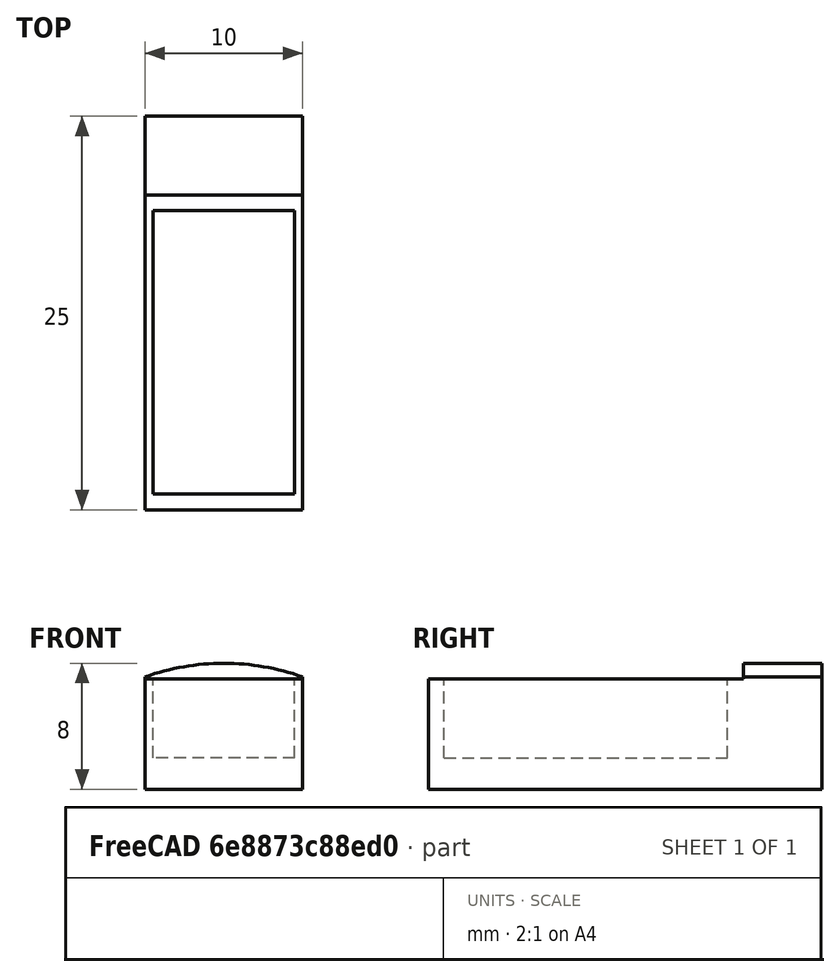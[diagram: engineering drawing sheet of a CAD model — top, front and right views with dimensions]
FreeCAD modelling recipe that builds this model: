
FCSTD DOCUMENT  (FreeCAD 0.16R4924 (Git))
Label: pin_v3
License: All rights reserved
LicenseURL: http://en.wikipedia.org/wiki/All_rights_reserved
objects: Part::Feature×9, Part::Box×3, Part::Cylinder×1, Part::MultiCommon×1, Part::MultiFuse×1, Part::Fuse×1, Part::Cut×1
note: 17 computed .brp shape members not serialized (recipe doc carries the construction recipe); baked Part::Feature solids carry a one-line shape summary decoded from their .brp

FEATURE [Part::Cylinder] Cylinder  label="rounded_top"
  Angle = 360
  Height = 30
  Placement = pos=(5,25,-7) rot=(1,0,0;1.5708rad)
  Radius = 15
FEATURE [Part::Box] Box  label="pin"
  Height = 8
  Length = 10
  Width = 30
FEATURE [Part::MultiCommon] Common  label="rounded pin"
  Shapes = -> [Cylinder,Box]
FEATURE [Part::Box] cube
  Height = 5
  Length = 18
  Placement = pos=(-9,-4.5,-2.5) rot=(0,0,1;0rad)
  Width = 9
FEATURE [Part::Feature] polyhedron
  Placement = pos=(-8.24512,0,2.5) rot=(0,0,1;0rad)
  shape: bbox 1.51 x 9 x 1.337 mm, 6 faces (baked)
FEATURE [Part::Feature] polyhedron001
  Placement = pos=(-6.24512,0,2.5) rot=(0,0,1;0rad)
  shape: bbox 1.51 x 9 x 1.337 mm, 6 faces (baked)
FEATURE [Part::Feature] polyhedron002
  Placement = pos=(-4.24512,0,2.5) rot=(0,0,1;0rad)
  shape: bbox 1.51 x 9 x 1.337 mm, 6 faces (baked)
FEATURE [Part::Feature] polyhedron003
  Placement = pos=(-2.24512,0,2.5) rot=(0,0,1;0rad)
  shape: bbox 1.51 x 9 x 1.337 mm, 6 faces (baked)
FEATURE [Part::Feature] polyhedron004
  Placement = pos=(-0.245118,0,2.5) rot=(0,0,1;0rad)
  shape: bbox 1.51 x 9 x 1.337 mm, 6 faces (baked)
FEATURE [Part::Feature] polyhedron005
  Placement = pos=(1.75488,0,2.5) rot=(0,0,1;0rad)
  shape: bbox 1.51 x 9 x 1.337 mm, 6 faces (baked)
FEATURE [Part::Feature] polyhedron006
  Placement = pos=(3.75488,0,2.5) rot=(0,0,1;0rad)
  shape: bbox 1.51 x 9 x 1.337 mm, 6 faces (baked)
FEATURE [Part::Feature] polyhedron007
  Placement = pos=(5.75488,0,2.5) rot=(0,0,1;0rad)
  shape: bbox 1.51 x 9 x 1.337 mm, 6 faces (baked)
FEATURE [Part::Feature] polyhedron008
  Placement = pos=(7.75488,0,2.5) rot=(0,0,1;0rad)
  shape: bbox 1.51 x 9 x 1.337 mm, 6 faces (baked)
FEATURE [Part::MultiFuse] Group
  Shapes = -> [polyhedron,polyhedron001,polyhedron002,polyhedron003,polyhedron004,polyhedron005,polyhedron006,polyhedron007,polyhedron008]
FEATURE [Part::Fuse] union  label="rack"
  Base = -> cube
  Placement = pos=(5,10,4.5) rot=(0,0,1;1.5708rad)
  Tool = -> Group
FEATURE [Part::Box] Box001  label="flat_top"
  Height = 10
  Length = 10
  Placement = pos=(0,0,7) rot=(0,0,1;0rad)
  Width = 20
FEATURE [Part::Cut] Cut
  Base = -> Common
  Tool = -> Box001
